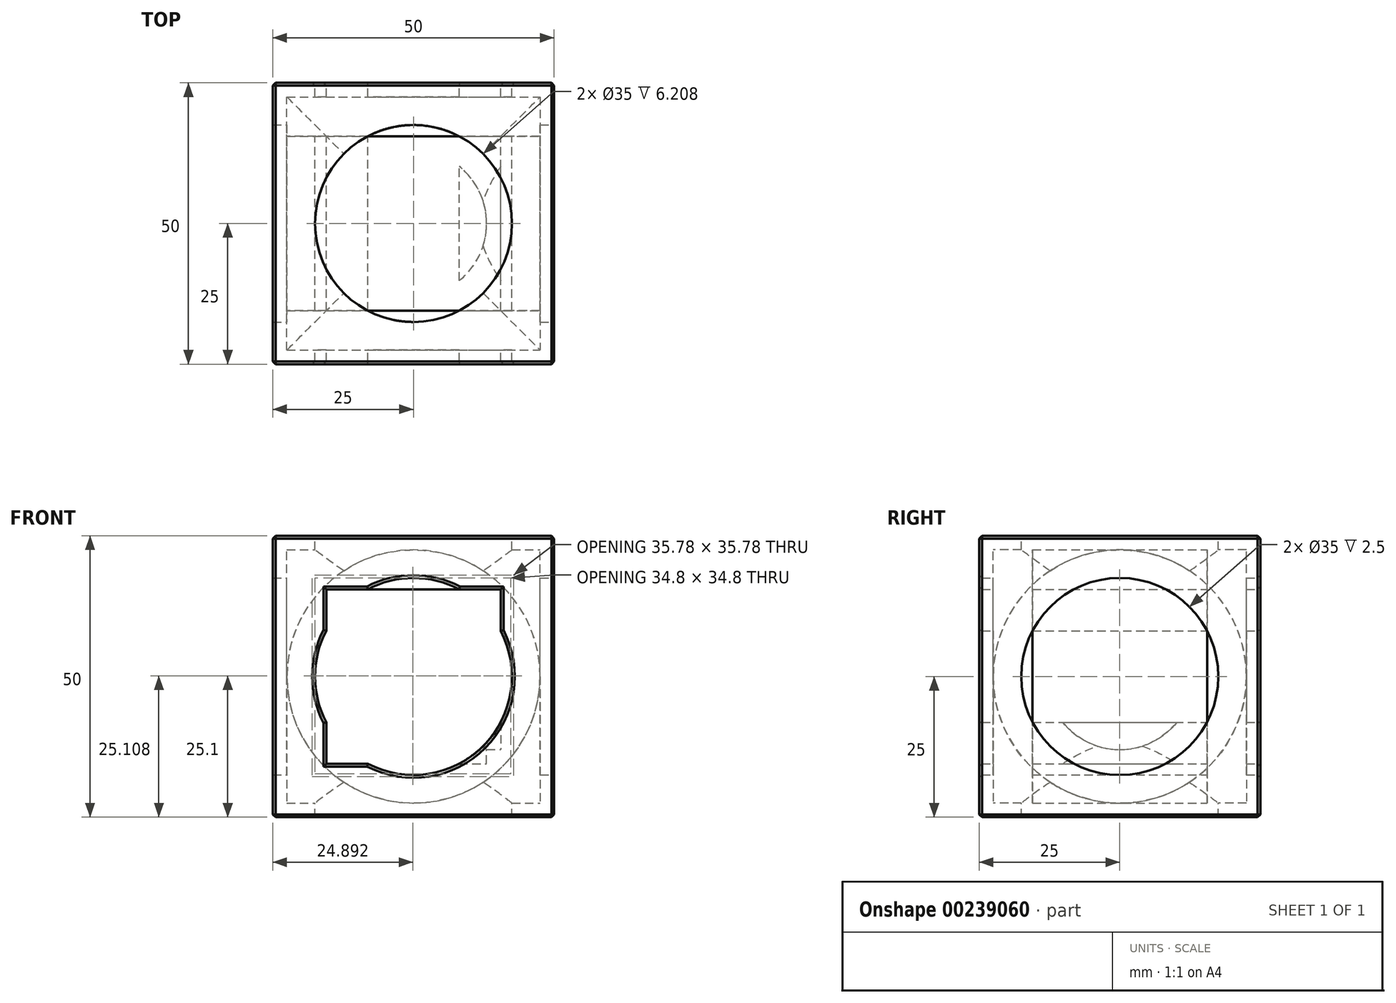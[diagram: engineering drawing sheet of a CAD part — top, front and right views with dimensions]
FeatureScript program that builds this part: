
annotation { "Feature Type Name" : "Feature", "Feature Type Description" : "" }
export const myFeature = defineFeature(function(context is Context, id is Id, definition is map)
    precondition{}
    {
        {
            var Q0;
            Q0=qCreatedBy(makeId("Front.planeOp"),FACE);
            var sketch = newSketch(context, id + "F0", { "sketchPlane" : qUnion([Q0])});
            skLineSegment(sketch, "E0.bottom", {"start": v(25, -25) * mm, "end": v(-25, -25) * mm});
            skLineSegment(sketch, "E0.top", {"start": v(25, 25) * mm, "end": v(-25, 25) * mm});
            skLineSegment(sketch, "E0.left", {"start": v(25, -25) * mm, "end": v(25, 25) * mm});
            skLineSegment(sketch, "E0.right", {"start": v(-25, -25) * mm, "end": v(-25, 25) * mm});
            skPoint(sketch, "E0.middle", {"position": v(0, 0) * mm});
            skCircle(sketch, "E1", {"center": v(0, 0) * mm, "radius": 17.5 * mm});
            skCircle(sketch, "E2", {"center": v(0, 0) * mm, "radius": 22.5 * mm});
            skLineSegment(sketch, "E3.bottom", {"start": v(-15.5, -15.5) * mm, "end": v(15.5, -15.5) * mm});
            skLineSegment(sketch, "E3.top", {"start": v(-15.5, 15.5) * mm, "end": v(15.5, 15.5) * mm});
            skLineSegment(sketch, "E3.left", {"start": v(-15.5, -15.5) * mm, "end": v(-15.5, 15.5) * mm});
            skLineSegment(sketch, "E3.right", {"start": v(15.5, -15.5) * mm, "end": v(15.5, 15.5) * mm});
            skCircle(sketch, "E4", {"center": v(0, 0) * mm, "radius": 13 * mm});
            skSolve(sketch);
        }
        {
            var Q0;
            Q0=makeQuery(id+"F0.imprint","IMPRINT",FACE,{"disambiguationData":[TD([[makeQuery(id+"F0.imprint","IMPRINT",EDGE,{"derivedFrom":sQuery(id+"F0.wireOp",EDGE,"E0.bottom")}),-1.0]])]});
            var Q1;
            Q1=makeQuery(id+"F0.imprint","IMPRINT",FACE,{"disambiguationData":[TD([[makeQuery(id+"F0.imprint","IMPRINT",EDGE,{"derivedFrom":sQuery(id+"F0.wireOp",EDGE,"ZFmpLQJs-m3o4-NlLn-QHJw-1qPJMhJcrLXY")}),-1.0]])]});
            var Q2;
            Q2=makeQuery(id+"F0.imprint","IMPRINT",FACE,{"disambiguationData":[TD([[makeQuery(id+"F0.imprint","IMPRINT",EDGE,{"derivedFrom":sQuery(id+"F0.wireOp",EDGE,"IJNPC6Xa-HIsr-ZxaT-OWxV-l6bE4DvLLeks")}),-1.0]])]});
            var Q3;
            Q3=makeQuery(id+"F0.imprint","IMPRINT",FACE,{"disambiguationData":[TD([[makeQuery(id+"F0.imprint","IMPRINT",EDGE,{"derivedFrom":sQuery(id+"F0.wireOp",EDGE,"IJNPC6Xa-HIsr-ZxaT-OWxV-l6bE4DvLLeks")}),1.0]])]});
            var Q4;
            Q4=makeQuery(id+"F0.imprint","IMPRINT",FACE,{"disambiguationData":[TD([[makeQuery(id+"F0.imprint","IMPRINT",EDGE,{"derivedFrom":sQuery(id+"F0.wireOp",EDGE,"E1")}),-1.0]])]});
            var Q5;
            {var subQ0=sQuery(id+"F0.wireOp",EDGE,"E3.top");var subQ1=sQuery(id+"F0.wireOp",EDGE,"E1");var subQ2=makeQuery(id+"F0.imprint","INTERSECT",VERTEX,{"disambiguationData":[OD(0.0)],"derivedFrom":[subQ1,subQ0]});Q5=makeQuery(id+"F0.imprint","IMPRINT",FACE,{"disambiguationData":[TD([[makeQuery(id+"F0.imprint","IMPRINT",EDGE,{"disambiguationData":[TD([[subQ2,1.0]])],"derivedFrom":subQ1}),-1.0]])]});}
            var Q6;
            {var subQ0=sQuery(id+"F0.wireOp",EDGE,"E3.bottom");var subQ1=sQuery(id+"F0.wireOp",EDGE,"E1");var subQ2=makeQuery(id+"F0.imprint","INTERSECT",VERTEX,{"disambiguationData":[OD(1.0)],"derivedFrom":[subQ1,subQ0]});Q6=makeQuery(id+"F0.imprint","IMPRINT",FACE,{"disambiguationData":[TD([[makeQuery(id+"F0.imprint","IMPRINT",EDGE,{"disambiguationData":[TD([[subQ2,-1.0]])],"derivedFrom":subQ1}),-1.0]])]});}
            var Q7;
            {var subQ0=sQuery(id+"F0.wireOp",EDGE,"E3.left");var subQ1=sQuery(id+"F0.wireOp",EDGE,"E1");var subQ2=makeQuery(id+"F0.imprint","INTERSECT",VERTEX,{"disambiguationData":[OD(1.0)],"derivedFrom":[subQ1,subQ0]});Q7=makeQuery(id+"F0.imprint","IMPRINT",FACE,{"disambiguationData":[TD([[makeQuery(id+"F0.imprint","IMPRINT",EDGE,{"disambiguationData":[TD([[subQ2,-1.0]])],"derivedFrom":subQ1}),-1.0]])]});}
            var Q8;
            {var subQ0=sQuery(id+"F0.wireOp",EDGE,"E3.top");var subQ1=sQuery(id+"F0.wireOp",EDGE,"E1");var subQ2=makeQuery(id+"F0.imprint","INTERSECT",VERTEX,{"disambiguationData":[OD(1.0)],"derivedFrom":[subQ1,subQ0]});Q8=makeQuery(id+"F0.imprint","IMPRINT",FACE,{"disambiguationData":[TD([[makeQuery(id+"F0.imprint","IMPRINT",EDGE,{"disambiguationData":[TD([[subQ2,-1.0]])],"derivedFrom":subQ1}),-1.0]])]});}
            extrude(context, id + "F1", {"entities" : qUnion([Q0, Q1, Q2, Q3, Q4, Q5, Q6, Q7, Q8]), "endBound" : BoundingType.SYMMETRIC, "depth" : 50 * mm});
        }
        {
            var Q0;
            Q0=makeQuery(id+"F1.opExtrude","CAP_FACE",FACE,{"disambiguationData":[OSD([sQuery(id+"F0.wireOp",EDGE,"E0.bottom"),sQuery(id+"F0.wireOp",EDGE,"E0.top"),sQuery(id+"F0.wireOp",EDGE,"E0.left"),sQuery(id+"F0.wireOp",EDGE,"E0.right")])],"isStart":false});
            var Q1;
            Q1=makeQuery(id+"F1.opExtrude","SWEPT_FACE",FACE,{"disambiguationData":[OSD([sQuery(id+"F0.wireOp",EDGE,"E0.top")])]});
            var Q2;
            Q2=makeQuery(id+"F1.opExtrude","CAP_FACE",FACE,{"disambiguationData":[OSD([sQuery(id+"F0.wireOp",EDGE,"E0.bottom"),sQuery(id+"F0.wireOp",EDGE,"E0.top"),sQuery(id+"F0.wireOp",EDGE,"E0.left"),sQuery(id+"F0.wireOp",EDGE,"E0.right")])],"isStart":true});
            var Q3;
            Q3=makeQuery(id+"F1.opExtrude","SWEPT_FACE",FACE,{"disambiguationData":[OSD([sQuery(id+"F0.wireOp",EDGE,"E0.bottom")])]});
            chamfer(context, id + "F2", {"entities" : qUnion([Q0, Q1, Q2, Q3]), "width" : .5 * mm, "tangentPropagation" : true});
        }
        {
            var Q0;
            Q0=qCreatedBy(makeId("Top.planeOp"),FACE);
            var sketch = newSketch(context, id + "F3", { "sketchPlane" : qUnion([Q0])});
            skLineSegment(sketch, "E5.bottom", {"start": v(25, -25) * mm, "end": v(-25, -25) * mm});
            skLineSegment(sketch, "E5.top", {"start": v(25, 25) * mm, "end": v(-25, 25) * mm});
            skLineSegment(sketch, "E5.left", {"start": v(25, -25) * mm, "end": v(25, 25) * mm});
            skLineSegment(sketch, "E5.right", {"start": v(-25, -25) * mm, "end": v(-25, 25) * mm});
            skPoint(sketch, "E5.middle", {"position": v(0, 0) * mm});
            skCircle(sketch, "E6", {"center": v(0, 0) * mm, "radius": 17.5 * mm});
            skSolve(sketch);
        }
        {
            var Q0;
            Q0=makeQuery(id+"F3.imprint","IMPRINT",FACE,{"disambiguationData":[TD([[makeQuery(id+"F3.imprint","IMPRINT",EDGE,{"derivedFrom":sQuery(id+"F3.wireOp",EDGE,"E6")}),1.0]])]});
            extrude(context, id + "F4", {"entities" : qUnion([Q0]), "operationType" : NewBodyOperationType.REMOVE, "endBound" : BoundingType.SYMMETRIC, "oppositeDirection" : true, "depth" : 50 * mm});
        }
        {
            var Q0;
            Q0=qCreatedBy(makeId("Right.planeOp"),FACE);
            var sketch = newSketch(context, id + "F5", { "sketchPlane" : qUnion([Q0])});
            skLineSegment(sketch, "E7.bottom", {"start": v(25, -25) * mm, "end": v(-25, -25) * mm});
            skLineSegment(sketch, "E7.top", {"start": v(25, 25) * mm, "end": v(-25, 25) * mm});
            skLineSegment(sketch, "E7.left", {"start": v(25, -25) * mm, "end": v(25, 25) * mm});
            skLineSegment(sketch, "E7.right", {"start": v(-25, -25) * mm, "end": v(-25, 25) * mm});
            skPoint(sketch, "E7.middle", {"position": v(0, 0) * mm});
            skCircle(sketch, "E8", {"center": v(0, 0) * mm, "radius": 17.5 * mm});
            skCircle(sketch, "E9", {"center": v(0, 0) * mm, "radius": 22.5 * mm});
            skSolve(sketch);
        }
        {
            var Q0;
            Q0=makeQuery(id+"F5.imprint","IMPRINT",FACE,{"disambiguationData":[TD([[makeQuery(id+"F5.imprint","IMPRINT",EDGE,{"derivedFrom":sQuery(id+"F5.wireOp",EDGE,"E8")}),1.0]])]});
            extrude(context, id + "F6", {"entities" : qUnion([Q0]), "operationType" : NewBodyOperationType.REMOVE, "endBound" : BoundingType.SYMMETRIC, "oppositeDirection" : true, "depth" : 50 * mm});
        }
        {
            var Q0;
            Q0=makeQuery(id+"F0.imprint","IMPRINT",FACE,{"disambiguationData":[TD([[makeQuery(id+"F0.imprint","IMPRINT",EDGE,{"derivedFrom":sQuery(id+"F0.wireOp",EDGE,"E1")}),-1.0]])]});
            var Q1;
            {var subQ0=sQuery(id+"F0.wireOp",EDGE,"E3.top");var subQ1=sQuery(id+"F0.wireOp",EDGE,"E1");var subQ2=makeQuery(id+"F0.imprint","INTERSECT",VERTEX,{"disambiguationData":[OD(0.0)],"derivedFrom":[subQ1,subQ0]});Q1=makeQuery(id+"F0.imprint","IMPRINT",FACE,{"disambiguationData":[TD([[makeQuery(id+"F0.imprint","IMPRINT",EDGE,{"disambiguationData":[TD([[subQ2,1.0]])],"derivedFrom":subQ1}),-1.0]])]});}
            var Q2;
            {var subQ0=sQuery(id+"F0.wireOp",EDGE,"E3.bottom");var subQ1=sQuery(id+"F0.wireOp",EDGE,"E1");var subQ2=makeQuery(id+"F0.imprint","INTERSECT",VERTEX,{"disambiguationData":[OD(1.0)],"derivedFrom":[subQ1,subQ0]});Q2=makeQuery(id+"F0.imprint","IMPRINT",FACE,{"disambiguationData":[TD([[makeQuery(id+"F0.imprint","IMPRINT",EDGE,{"disambiguationData":[TD([[subQ2,-1.0]])],"derivedFrom":subQ1}),-1.0]])]});}
            var Q3;
            {var subQ0=sQuery(id+"F0.wireOp",EDGE,"E3.left");var subQ1=sQuery(id+"F0.wireOp",EDGE,"E1");var subQ2=makeQuery(id+"F0.imprint","INTERSECT",VERTEX,{"disambiguationData":[OD(1.0)],"derivedFrom":[subQ1,subQ0]});Q3=makeQuery(id+"F0.imprint","IMPRINT",FACE,{"disambiguationData":[TD([[makeQuery(id+"F0.imprint","IMPRINT",EDGE,{"disambiguationData":[TD([[subQ2,-1.0]])],"derivedFrom":subQ1}),-1.0]])]});}
            var Q4;
            {var subQ0=sQuery(id+"F0.wireOp",EDGE,"E3.top");var subQ1=sQuery(id+"F0.wireOp",EDGE,"E1");var subQ2=makeQuery(id+"F0.imprint","INTERSECT",VERTEX,{"disambiguationData":[OD(1.0)],"derivedFrom":[subQ1,subQ0]});Q4=makeQuery(id+"F0.imprint","IMPRINT",FACE,{"disambiguationData":[TD([[makeQuery(id+"F0.imprint","IMPRINT",EDGE,{"disambiguationData":[TD([[subQ2,-1.0]])],"derivedFrom":subQ1}),-1.0]])]});}
            extrude(context, id + "F7", {"entities" : qUnion([Q0, Q1, Q2, Q3, Q4]), "operationType" : NewBodyOperationType.REMOVE, "endBound" : BoundingType.SYMMETRIC, "oppositeDirection" : true, "depth" : 45 * mm});
        }
        {
            var Q0;
            Q0=makeQuery(id+"F5.imprint","IMPRINT",FACE,{"disambiguationData":[TD([[makeQuery(id+"F5.imprint","IMPRINT",EDGE,{"derivedFrom":sQuery(id+"F5.wireOp",EDGE,"E8")}),-1.0]])]});
            extrude(context, id + "F8", {"entities" : qUnion([Q0]), "operationType" : NewBodyOperationType.REMOVE, "endBound" : BoundingType.SYMMETRIC, "oppositeDirection" : true, "depth" : 45 * mm});
        }
        {
            var Q0;
            {var subQ0=sQuery(id+"F0.wireOp",EDGE,"E3.top");var subQ1=sQuery(id+"F0.wireOp",EDGE,"E1");var subQ2=makeQuery(id+"F0.imprint","INTERSECT",VERTEX,{"disambiguationData":[OD(1.0)],"derivedFrom":[subQ1,subQ0]});Q0=makeQuery(id+"F0.imprint","IMPRINT",FACE,{"disambiguationData":[TD([[makeQuery(id+"F0.imprint","IMPRINT",EDGE,{"disambiguationData":[TD([[subQ2,-1.0]])],"derivedFrom":subQ1}),-1.0]])]});}
            var Q1;
            {var subQ1=sQuery(id+"F0.wireOp",EDGE,"E1");var subQ8=sQuery(id+"F0.wireOp",EDGE,"E3.top");var subQ11=makeQuery(id+"F0.imprint","INTERSECT",VERTEX,{"disambiguationData":[OD(0.0)],"derivedFrom":[subQ1,subQ8]});Q1=makeQuery(id+"F0.imprint","IMPRINT",FACE,{"disambiguationData":[TD([[makeQuery(id+"F0.imprint","IMPRINT",EDGE,{"disambiguationData":[TD([[subQ11,1.0]])],"derivedFrom":subQ1}),1.0]])]});}
            var Q2;
            {var subQ0=sQuery(id+"F0.wireOp",EDGE,"E3.left");var subQ1=sQuery(id+"F0.wireOp",EDGE,"E1");var subQ2=makeQuery(id+"F0.imprint","INTERSECT",VERTEX,{"disambiguationData":[OD(1.0)],"derivedFrom":[subQ1,subQ0]});Q2=makeQuery(id+"F0.imprint","IMPRINT",FACE,{"disambiguationData":[TD([[makeQuery(id+"F0.imprint","IMPRINT",EDGE,{"disambiguationData":[TD([[subQ2,-1.0]])],"derivedFrom":subQ1}),-1.0]])]});}
            var Q3;
            {var subQ0=sQuery(id+"F0.wireOp",EDGE,"E3.bottom");var subQ1=sQuery(id+"F0.wireOp",EDGE,"E1");var subQ2=makeQuery(id+"F0.imprint","INTERSECT",VERTEX,{"disambiguationData":[OD(1.0)],"derivedFrom":[subQ1,subQ0]});Q3=makeQuery(id+"F0.imprint","IMPRINT",FACE,{"disambiguationData":[TD([[makeQuery(id+"F0.imprint","IMPRINT",EDGE,{"disambiguationData":[TD([[subQ2,-1.0]])],"derivedFrom":subQ1}),-1.0]])]});}
            var Q4;
            {var subQ0=sQuery(id+"F0.wireOp",EDGE,"E3.top");var subQ1=sQuery(id+"F0.wireOp",EDGE,"E1");var subQ2=makeQuery(id+"F0.imprint","INTERSECT",VERTEX,{"disambiguationData":[OD(0.0)],"derivedFrom":[subQ1,subQ0]});Q4=makeQuery(id+"F0.imprint","IMPRINT",FACE,{"disambiguationData":[TD([[makeQuery(id+"F0.imprint","IMPRINT",EDGE,{"disambiguationData":[TD([[subQ2,1.0]])],"derivedFrom":subQ1}),-1.0]])]});}
            extrude(context, id + "F9", {"entities" : qUnion([Q0, Q1, Q2, Q3, Q4]), "endBound" : BoundingType.SYMMETRIC, "depth" : 31 * mm});
        }
        {
            var Q0;
            Q0=qCreatedBy(makeId("Right.planeOp"),FACE);
            var sketch = newSketch(context, id + "F10", { "sketchPlane" : qUnion([Q0])});
            skCircle(sketch, "E10", {"center": v(0, 0) * mm, "radius": 13 * mm});
            skSolve(sketch);
        }
        {
            var Q0;
            Q0=makeQuery(id+"F10.imprint","IMPRINT",FACE,{"disambiguationData":[TD([[makeQuery(id+"F10.imprint","IMPRINT",EDGE,{"derivedFrom":sQuery(id+"F10.wireOp",EDGE,"E10")}),1.0]])]});
            extrude(context, id + "F11", {"entities" : qUnion([Q0]), "operationType" : NewBodyOperationType.REMOVE, "endBound" : BoundingType.SYMMETRIC, "oppositeDirection" : true, "depth" : 31 * mm});
        }
        {
            var Q0;
            Q0=qCreatedBy(makeId("Top.planeOp"),FACE);
            var sketch = newSketch(context, id + "F12", { "sketchPlane" : qUnion([Q0])});
            skCircle(sketch, "E11", {"center": v(0, 0) * mm, "radius": 13 * mm});
            skSolve(sketch);
        }
        {
            var Q0;
            Q0=makeQuery(id+"F12.imprint","IMPRINT",FACE,{"disambiguationData":[TD([[makeQuery(id+"F12.imprint","IMPRINT",EDGE,{"derivedFrom":sQuery(id+"F12.wireOp",EDGE,"E11")}),1.0]])]});
            extrude(context, id + "F13", {"entities" : qUnion([Q0]), "operationType" : NewBodyOperationType.REMOVE, "endBound" : BoundingType.SYMMETRIC, "oppositeDirection" : true, "depth" : 31 * mm});
        }
    });
